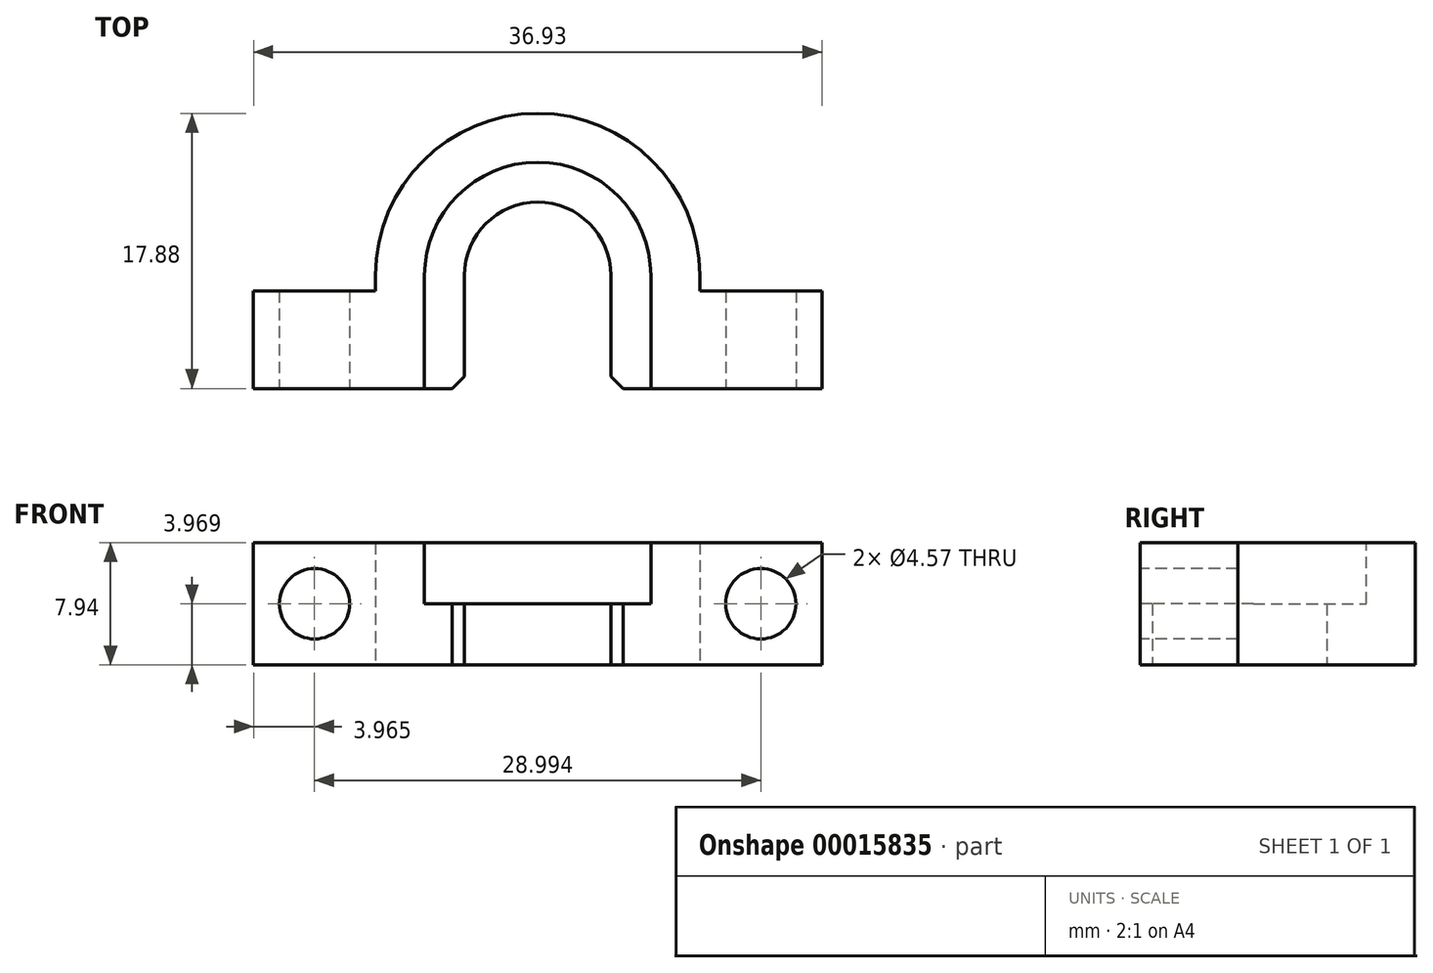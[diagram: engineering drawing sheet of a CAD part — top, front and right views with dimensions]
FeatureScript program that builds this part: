
annotation { "Feature Type Name" : "Feature", "Feature Type Description" : "" }
export const myFeature = defineFeature(function(context is Context, id is Id, definition is map)
    precondition{}
    {
        {
            var Q0;
            Q0=qCreatedBy(makeId("Top.planeOp"),FACE);
            var sketch = newSketch(context, id + "F0", { "sketchPlane" : qUnion([Q0])});
            skLineSegment(sketch, "E0", {"start": v(0, 0) * mm, "end": v(-5.77, 0) * mm, "construction": true});
            skLineSegment(sketch, "E1", {"start": v(-5.77, 0) * mm, "end": v(-15.3, 0) * mm, "construction": true});
            skLineSegment(sketch, "E2", {"start": v(-15.3, 0) * mm, "end": v(-21.06, 0) * mm, "construction": true});
            skLineSegment(sketch, "E3", {"start": v(0, 0) * mm, "end": v(0, -1) * mm});
            skLineSegment(sketch, "E4", {"start": v(-5.77, 0) * mm, "end": v(-5.77, -7.35) * mm});
            skLineSegment(sketch, "E5", {"start": v(0, -1) * mm, "end": v(7.94, -1) * mm});
            skLineSegment(sketch, "E6", {"start": v(7.94, -1) * mm, "end": v(7.94, -7.35) * mm});
            skLineSegment(sketch, "E7", {"start": v(7.94, -7.35) * mm, "end": v(-5.77, -7.35) * mm});
            skLineSegment(sketch, "E8", {"start": v(-15.3, 0) * mm, "end": v(-15.3, -7.35) * mm});
            skLineSegment(sketch, "E9", {"start": v(-15.3, -7.35) * mm, "end": v(-29, -7.35) * mm});
            skLineSegment(sketch, "E10", {"start": v(-29, -7.35) * mm, "end": v(-29, -1) * mm});
            skLineSegment(sketch, "E11", {"start": v(-29, -1) * mm, "end": v(-21.06, -1) * mm});
            skLineSegment(sketch, "E12", {"start": v(-21.06, -1) * mm, "end": v(-21.06, 0) * mm});
            skArc(sketch, "E13", {"start": v(-5.77, 0) * mm, "mid": v(-10.53, 4.76) * mm, "end": v(-15.3, 0) * mm});
            skArc(sketch, "E14", {"start": v(0, 0) * mm, "mid": v(-10.53, 10.53) * mm, "end": v(-21.06, 0) * mm});
            skSolve(sketch);
        }
        {
            var Q0;
            Q0=qSketchRegion(id+"F0",true);
            extrude(context, id + "F1", {"entities" : qUnion([Q0]), "depth" : 7.94 * mm});
        }
        {
            var Q0;
            Q0=makeQuery(id+"F1.opExtrude","SWEPT_FACE",FACE,{"disambiguationData":[OSD([sQuery(id+"F0.wireOp",EDGE,"E9")])]});
            var sketch = newSketch(context, id + "F2", { "sketchPlane" : qUnion([Q0])});
            skLineSegment(sketch, "E15", {"start": v(-29, 3.97) * mm, "end": v(-25.03, 3.97) * mm});
            skLineSegment(sketch, "E16", {"start": v(7.94, 3.97) * mm, "end": v(3.97, 3.97) * mm});
            skCircle(sketch, "E17", {"center": v(-25.03, 3.97) * mm, "radius": 2.29 * mm});
            skCircle(sketch, "E18", {"center": v(3.97, 3.97) * mm, "radius": 2.29 * mm});
            skSolve(sketch);
        }
        {
            var Q0;
            Q0=qSketchRegion(id+"F2",true);
            var Q1;
            Q1=makeQuery(id+"F1.opExtrude","SWEPT_FACE",FACE,{"disambiguationData":[OSD([sQuery(id+"F0.wireOp",EDGE,"E11")])]});
            extrude(context, id + "F3", {"entities" : qUnion([Q0]), "operationType" : NewBodyOperationType.REMOVE, "endBound" : BoundingType.UP_TO_SURFACE, "oppositeDirection" : true, "endBoundEntityFace" : qUnion([Q1]), "depth" : 25.4 * mm});
        }
        {
            var Q0;
            Q0=makeQuery(id+"F1.opExtrude","CAP_FACE",FACE,{"disambiguationData":[OSD([sQuery(id+"F0.wireOp",EDGE,"E3"),sQuery(id+"F0.wireOp",EDGE,"E4"),sQuery(id+"F0.wireOp",EDGE,"E5"),sQuery(id+"F0.wireOp",EDGE,"E6"),sQuery(id+"F0.wireOp",EDGE,"E7"),sQuery(id+"F0.wireOp",EDGE,"E8"),sQuery(id+"F0.wireOp",EDGE,"E9"),sQuery(id+"F0.wireOp",EDGE,"E10"),sQuery(id+"F0.wireOp",EDGE,"E11"),sQuery(id+"F0.wireOp",EDGE,"E12"),sQuery(id+"F0.wireOp",EDGE,"E13"),sQuery(id+"F0.wireOp",EDGE,"E14")])],"isStart":false});
            var sketch = newSketch(context, id + "F4", { "sketchPlane" : qUnion([Q0])});
            skLineSegment(sketch, "E19.bottom", {"start": v(-15.3, 0) * mm, "end": v(-17.88, 0) * mm});
            skLineSegment(sketch, "E19.top", {"start": v(-15.3, -7.35) * mm, "end": v(-17.88, -7.35) * mm});
            skLineSegment(sketch, "E19.left", {"start": v(-15.3, 0) * mm, "end": v(-15.3, -7.35) * mm});
            skLineSegment(sketch, "E19.right", {"start": v(-17.88, 0) * mm, "end": v(-17.88, -7.35) * mm});
            skLineSegment(sketch, "E20.bottom", {"start": v(-5.77, 0) * mm, "end": v(-3.18, 0) * mm});
            skLineSegment(sketch, "E20.top", {"start": v(-5.77, -7.35) * mm, "end": v(-3.17, -7.35) * mm});
            skLineSegment(sketch, "E20.left", {"start": v(-5.77, 0) * mm, "end": v(-5.77, -7.35) * mm});
            skLineSegment(sketch, "E20.right", {"start": v(-3.18, 0) * mm, "end": v(-3.17, -7.35) * mm});
            skArc(sketch, "E21", {"start": v(-5.77, 0) * mm, "mid": v(-10.53, 4.76) * mm, "end": v(-15.3, 0) * mm});
            skArc(sketch, "E22", {"start": v(-3.18, 0) * mm, "mid": v(-10.53, 7.35) * mm, "end": v(-17.88, 0) * mm});
            skLineSegment(sketch, "E23", {"start": v(-3.18, 0) * mm, "end": v(0, 0) * mm, "construction": true});
            skSolve(sketch);
        }
        {
            var Q0;
            Q0 = qSketchRegion(id + "F4", true);
            extrude(context, id + "F5", {"entities" : qUnion([Q0]), "operationType" : NewBodyOperationType.REMOVE, "oppositeDirection" : true, "depth" : 3.97 * mm});
        }
        {
            var Q0;
            Q0=makeQuery(id+"F1.opExtrude","SWEPT_EDGE",EDGE,{"disambiguationData":[OSD([sQuery(id+"F0.wireOp",EDGE,"E8"),sQuery(id+"F0.wireOp",EDGE,"E9")])]});
            var Q1;
            Q1=makeQuery(id+"F1.opExtrude","SWEPT_EDGE",EDGE,{"disambiguationData":[OSD([sQuery(id+"F0.wireOp",EDGE,"E4"),sQuery(id+"F0.wireOp",EDGE,"E7")])]});
            chamfer(context, id + "F6", {"entities" : qUnion([Q0, Q1]), "width" : 0.8 * mm, "tangentPropagation" : true});
        }
    });
